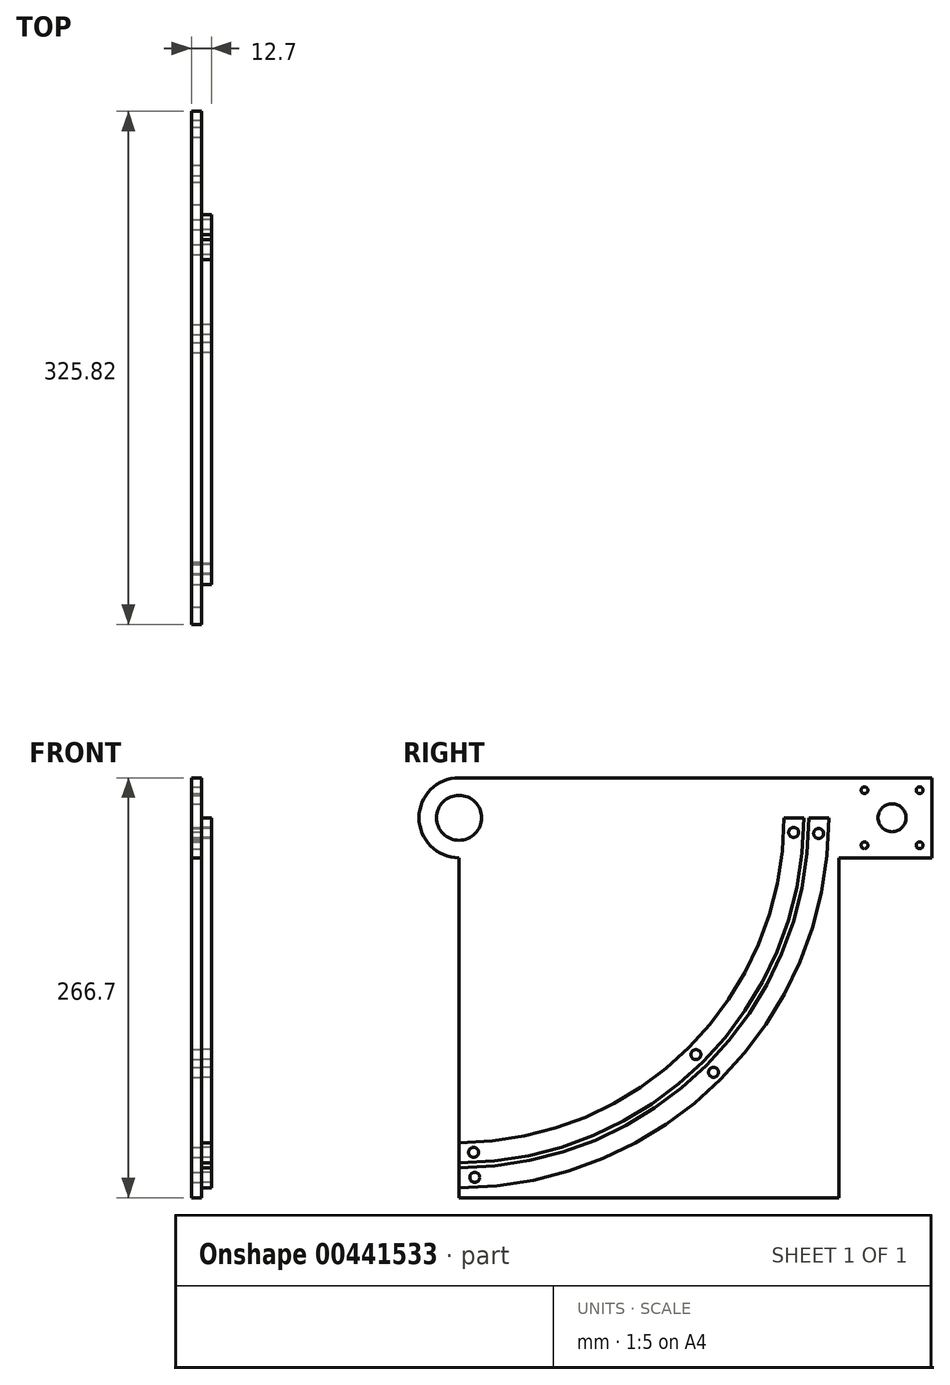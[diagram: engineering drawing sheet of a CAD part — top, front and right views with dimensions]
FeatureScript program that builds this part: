
annotation { "Feature Type Name" : "Feature", "Feature Type Description" : "" }
export const myFeature = defineFeature(function(context is Context, id is Id, definition is map)
    precondition{}
    {
        {
            var Q0;
            Q0=qCreatedBy(makeId("Right.planeOp"),FACE);
            var sketch = newSketch(context, id + "F0", { "sketchPlane" : qUnion([Q0])});
            skCircle(sketch, "E0", {"center": v(-150.42, 241.3) * mm, "radius": 25.4 * mm});
            skCircle(sketch, "E1", {"center": v(-150.42, 241.3) * mm, "radius": 14.29 * mm});
            skLineSegment(sketch, "E2.bottom", {"start": v(-150.42, 241.3) * mm, "end": v(90.88, 241.3) * mm});
            skLineSegment(sketch, "E2.top", {"start": v(-150.42, 0) * mm, "end": v(90.88, 0) * mm});
            skLineSegment(sketch, "E2.left", {"start": v(-150.42, 241.3) * mm, "end": v(-150.42, 0) * mm});
            skLineSegment(sketch, "E2.right", {"start": v(90.88, 241.3) * mm, "end": v(90.88, 0) * mm});
            skCircle(sketch, "E3", {"center": v(124.6, 241.3) * mm, "radius": 8.9 * mm});
            skLineSegment(sketch, "E4.bottom", {"start": v(142.1, 258.8) * mm, "end": v(107.1, 258.8) * mm, "construction": true});
            skLineSegment(sketch, "E4.top", {"start": v(142.1, 223.8) * mm, "end": v(107.1, 223.8) * mm, "construction": true});
            skLineSegment(sketch, "E4.left", {"start": v(142.1, 258.8) * mm, "end": v(142.1, 223.8) * mm, "construction": true});
            skLineSegment(sketch, "E4.right", {"start": v(107.1, 258.8) * mm, "end": v(107.1, 223.8) * mm, "construction": true});
            skCircle(sketch, "E5", {"center": v(142.1, 258.8) * mm, "radius": 2.16 * mm});
            skCircle(sketch, "E6", {"center": v(142.1, 223.8) * mm, "radius": 2.16 * mm});
            skCircle(sketch, "E7", {"center": v(107.1, 223.8) * mm, "radius": 2.16 * mm});
            skCircle(sketch, "E8", {"center": v(107.1, 258.8) * mm, "radius": 2.16 * mm});
            skArc(sketch, "E9", {"start": v(-150.42, 22.22) * mm, "mid": v(4.5, 86.4) * mm, "end": v(68.66, 241.3) * mm});
            skArc(sketch, "E10.0", {"start": v(-150.42, 12.7) * mm, "mid": v(11.23, 79.66) * mm, "end": v(78.18, 241.3) * mm, "construction": true});
            skArc(sketch, "E11.0", {"start": v(-150.42, 28.57) * mm, "mid": v(0, 90.88) * mm, "end": v(62.3, 241.3) * mm, "construction": true});
            skCircle(sketch, "E12", {"center": v(-141.14, 28.78) * mm, "radius": 3.18 * mm});
            skCircle(sketch, "E13", {"center": v(-140.45, 12.92) * mm, "radius": 3.18 * mm});
            skCircle(sketch, "E14", {"center": v(0, 90.88) * mm, "radius": 3.18 * mm});
            skCircle(sketch, "E15", {"center": v(11.23, 79.66) * mm, "radius": 3.18 * mm});
            skCircle(sketch, "E16", {"center": v(62.1, 232.02) * mm, "radius": 3.18 * mm});
            skCircle(sketch, "E17", {"center": v(77.96, 231.33) * mm, "radius": 3.18 * mm});
            skLineSegment(sketch, "E18", {"start": v(-150.42, 241.3) * mm, "end": v(77.96, 231.33) * mm, "construction": true});
            skLineSegment(sketch, "E19", {"start": v(11.23, 79.66) * mm, "end": v(-150.42, 241.3) * mm, "construction": true});
            skLineSegment(sketch, "E20", {"start": v(-140.45, 12.92) * mm, "end": v(-150.42, 241.3) * mm, "construction": true});
            skArc(sketch, "E21.0", {"start": v(-150.42, 34.92) * mm, "mid": v(-4.5, 95.37) * mm, "end": v(55.96, 241.3) * mm});
            skArc(sketch, "E22.0", {"start": v(-150.42, 19.05) * mm, "mid": v(6.74, 84.15) * mm, "end": v(71.83, 241.3) * mm});
            skArc(sketch, "E23.0", {"start": v(-150.42, 6.35) * mm, "mid": v(15.72, 75.17) * mm, "end": v(84.53, 241.3) * mm});
            skPoint(sketch, "E24", {"position": v(104.11, 244.05) * mm});
            skLineSegment(sketch, "E25", {"start": v(124.6, 241.3) * mm, "end": v(90.88, 241.3) * mm, "construction": true});
            skLineSegment(sketch, "E26.bottom", {"start": v(90.88, 215.9) * mm, "end": v(150, 215.9) * mm});
            skLineSegment(sketch, "E26.top", {"start": v(90.88, 266.7) * mm, "end": v(150, 266.7) * mm});
            skLineSegment(sketch, "E26.left", {"start": v(90.88, 215.9) * mm, "end": v(90.88, 266.7) * mm});
            skLineSegment(sketch, "E26.right", {"start": v(150, 215.9) * mm, "end": v(150, 266.7) * mm});
            skPoint(sketch, "E27", {"position": v(90.88, 241.3) * mm});
            skLineSegment(sketch, "E28", {"start": v(90.88, 266.7) * mm, "end": v(-150.42, 266.7) * mm});
            skSolve(sketch);
        }
        {
            var Q0;
            {var subQ5=sQuery(id+"F0.wireOp",EDGE,"E0");var subQ8=makeQuery(id+"F0.imprint","INTERSECT",VERTEX,{"derivedFrom":[subQ5,sQuery(id+"F0.wireOp",EDGE,"E28")]});Q0=makeQuery(id+"F0.imprint","IMPRINT",FACE,{"disambiguationData":[TD([[makeQuery(id+"F0.imprint","IMPRINT",EDGE,{"disambiguationData":[TD([[subQ8,1.0]])],"derivedFrom":subQ5}),1.0]])]});}
            var Q1;
            {var subQ0=sQuery(id+"F0.wireOp",EDGE,"E2.left");var subQ1=sQuery(id+"F0.wireOp",EDGE,"E0");var subQ2=makeQuery(id+"F0.imprint","INTERSECT",VERTEX,{"derivedFrom":[subQ1,subQ0]});Q1=makeQuery(id+"F0.imprint","IMPRINT",FACE,{"disambiguationData":[TD([[makeQuery(id+"F0.imprint","IMPRINT",EDGE,{"disambiguationData":[TD([[subQ2,-1.0]])],"derivedFrom":subQ1}),1.0]])]});}
            var Q2;
            {var subQ4=sQuery(id+"F0.wireOp",EDGE,"E28");Q2=makeQuery(id+"F0.imprint","IMPRINT",FACE,{"disambiguationData":[TD([[makeQuery(id+"F0.imprint","IMPRINT",EDGE,{"derivedFrom":subQ4}),1.0]])]});}
            var Q3;
            Q3=makeQuery(id+"F0.imprint","IMPRINT",FACE,{"disambiguationData":[TD([[makeQuery(id+"F0.imprint","IMPRINT",EDGE,{"derivedFrom":sQuery(id+"F0.wireOp",EDGE,"E3")}),-1.0]])]});
            var Q4;
            {var subQ2=sQuery(id+"F0.wireOp",EDGE,"E2.top");Q4=makeQuery(id+"F0.imprint","IMPRINT",FACE,{"disambiguationData":[TD([[makeQuery(id+"F0.imprint","IMPRINT",EDGE,{"derivedFrom":subQ2}),1.0]])]});}
            var Q5;
            Q5=makeQuery(id+"F0.imprint","IMPRINT",FACE,{"disambiguationData":[TD([[makeQuery(id+"F0.imprint","IMPRINT",EDGE,{"derivedFrom":sQuery(id+"F0.wireOp",EDGE,"E13")}),-1.0]])]});
            var Q6;
            {var subQ0=sQuery(id+"F0.wireOp",EDGE,"E9");Q6=makeQuery(id+"F0.imprint","IMPRINT",FACE,{"disambiguationData":[TD([[makeQuery(id+"F0.imprint","IMPRINT",EDGE,{"derivedFrom":subQ0}),-1.0]])]});}
            var Q7;
            {var subQ0=sQuery(id+"F0.wireOp",EDGE,"E9");Q7=makeQuery(id+"F0.imprint","IMPRINT",FACE,{"disambiguationData":[TD([[makeQuery(id+"F0.imprint","IMPRINT",EDGE,{"derivedFrom":subQ0}),1.0]])]});}
            var Q8;
            {var subQ5=sQuery(id+"F0.wireOp",EDGE,"E21.0");Q8=makeQuery(id+"F0.imprint","IMPRINT",FACE,{"disambiguationData":[TD([[makeQuery(id+"F0.imprint","IMPRINT",EDGE,{"derivedFrom":subQ5}),1.0]])]});}
            extrude(context, id + "F1", {"entities" : qUnion([Q0, Q1, Q2, Q3, Q4, Q5, Q6, Q7, Q8]), "oppositeDirection" : true, "depth" : 6.35 * mm, "offsetDistance" : 25.4 * mm});
        }
        {
            var Q0;
            {var subQ0=sQuery(id+"F0.wireOp",EDGE,"E9");Q0=makeQuery(id+"F0.imprint","IMPRINT",FACE,{"disambiguationData":[TD([[makeQuery(id+"F0.imprint","IMPRINT",EDGE,{"derivedFrom":subQ0}),1.0]])]});}
            extrude(context, id + "F2", {"entities" : qUnion([Q0]), "depth" : 6.35 * mm, "offsetDistance" : 25.4 * mm});
        }
        {
            var Q0;
            Q0=makeQuery(id+"F0.imprint","IMPRINT",FACE,{"disambiguationData":[TD([[makeQuery(id+"F0.imprint","IMPRINT",EDGE,{"derivedFrom":sQuery(id+"F0.wireOp",EDGE,"E13")}),-1.0]])]});
            extrude(context, id + "F3", {"entities" : qUnion([Q0]), "depth" : 6.35 * mm, "offsetDistance" : 25.4 * mm});
        }
    });
